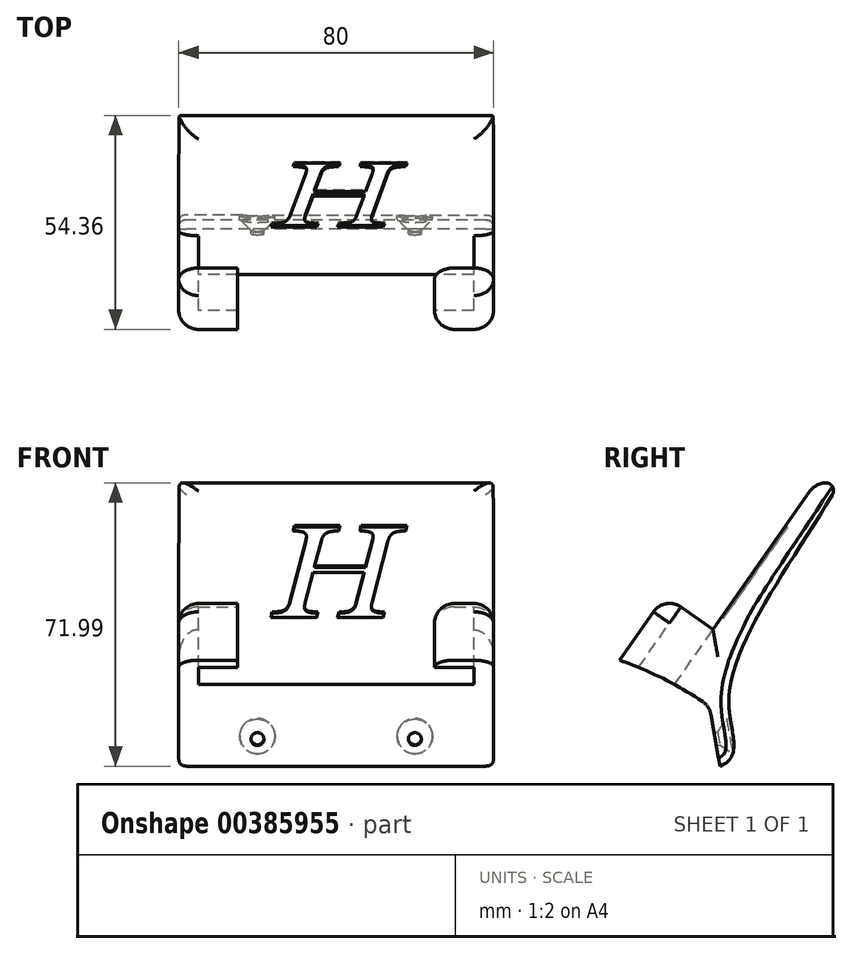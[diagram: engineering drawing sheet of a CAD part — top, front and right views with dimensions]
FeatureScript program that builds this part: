
annotation { "Feature Type Name" : "Feature", "Feature Type Description" : "" }
export const myFeature = defineFeature(function(context is Context, id is Id, definition is map)
    precondition{}
    {
        {
            var Q0;
            Q0=qCreatedBy(makeId("Right.planeOp"),FACE);
            var sketch = newSketch(context, id + "F0", { "sketchPlane" : qUnion([Q0])});
            skCircle(sketch, "E0", {"center": v(0, 0) * mm, "radius": 92 * mm});
            skLineSegment(sketch, "E1", {"start": v(53, 75.2) * mm, "end": v(53, 0) * mm});
            skLineSegment(sketch, "E2", {"start": v(0, 92) * mm, "end": v(0, 0) * mm});
            skLineSegment(sketch, "E3", {"start": v(0, 0) * mm, "end": v(53, 0) * mm});
            skLineSegment(sketch, "E4", {"start": v(41.65, 103.3) * mm, "end": v(53.94, 94.68) * mm});
            skLineSegment(sketch, "E5", {"start": v(53.94, 94.68) * mm, "end": v(44.15, 80.71) * mm});
            skLineSegment(sketch, "E6", {"start": v(53.94, 94.68) * mm, "end": v(81.44, 133.95) * mm});
            skLineSegment(sketch, "E7", {"start": v(81.44, 133.95) * mm, "end": v(85.54, 131.08) * mm});
            skLineSegment(sketch, "E8", {"start": v(53, 75.2) * mm, "end": v(61, 30.2) * mm});
            skLineSegment(sketch, "E9", {"start": v(41.65, 103.3) * mm, "end": v(30.18, 86.91) * mm});
            skFitSpline(sketch, "E10", {"points": [v(85.54, 131.08) * mm, v(57.95, 76.28) * mm, v(55.7, 59.99) * mm], "startDerivative": vector(-56.96, -95.44) * mm, "endDerivative": vector(-55.5, -22.93) * mm});
            skLineSegment(sketch, "E11", {"start": v(57.95, 76.28) * mm, "end": v(65.27, 35.08) * mm});
            skSolve(sketch);
        }
        {
            var Q0;
            {var subQ0=sQuery(id+"F0.wireOp",EDGE,"E1");var subQ1=sQuery(id+"F0.wireOp",EDGE,"E0");var subQ2=makeQuery(id+"F0.imprint","INTERSECT",VERTEX,{"derivedFrom":[subQ1,subQ0]});Q0=makeQuery(id+"F0.imprint","IMPRINT",FACE,{"disambiguationData":[TD([[makeQuery(id+"F0.imprint","IMPRINT",EDGE,{"disambiguationData":[TD([[subQ2,1.0]])],"derivedFrom":subQ1}),1.0]])]});}
            var Q1;
            {var subQ2=sQuery(id+"F0.wireOp",EDGE,"E5");Q1=makeQuery(id+"F0.imprint","IMPRINT",FACE,{"disambiguationData":[TD([[makeQuery(id+"F0.imprint","IMPRINT",EDGE,{"derivedFrom":subQ2}),1.0]])]});}
            var Q2;
            {var subQ0=sQuery(id+"F0.wireOp",EDGE,"VzTdmG4M-RMvp-aOg5-erqJ-xc0UWDuZk2gF");Q2=makeQuery(id+"F0.imprint","IMPRINT",FACE,{"disambiguationData":[TD([[makeQuery(id+"F0.imprint","IMPRINT",EDGE,{"derivedFrom":subQ0}),-1.0]])]});}
            var Q3;
            Q3=makeQuery(id+"F0.imprint","IMPRINT",FACE,{"disambiguationData":[TD([[makeQuery(id+"F0.imprint","IMPRINT",EDGE,{"derivedFrom":sQuery(id+"F0.wireOp",EDGE,"E4")}),-1.0]])]});
            extrude(context, id + "F1", {"entities" : qUnion([Q0, Q1, Q2, Q3]), "endBound" : BoundingType.SYMMETRIC, "depth" : 80 * mm});
        }
        {
            var Q0;
            Q0=makeQuery(id+"F1.opExtrude","SWEPT_FACE",FACE,{"disambiguationData":[OSD([sQuery(id+"F0.wireOp",EDGE,"E4")])]});
            var sketch = newSketch(context, id + "F2", { "sketchPlane" : qUnion([Q0])});
            skLineSegment(sketch, "E12.bottom", {"start": v(-35, -10.15) * mm, "end": v(35, -10.15) * mm});
            skLineSegment(sketch, "E12.top", {"start": v(-35, -20.15) * mm, "end": v(35, -20.15) * mm});
            skLineSegment(sketch, "E12.left", {"start": v(-35, -10.15) * mm, "end": v(-35, -20.15) * mm});
            skLineSegment(sketch, "E12.right", {"start": v(35, -10.15) * mm, "end": v(35, -20.15) * mm});
            skLineSegment(sketch, "E13.bottom", {"start": v(-25, -20.15) * mm, "end": v(25, -20.15) * mm});
            skLineSegment(sketch, "E13.top", {"start": v(-25, -25.15) * mm, "end": v(25, -25.15) * mm});
            skLineSegment(sketch, "E13.left", {"start": v(-25, -20.15) * mm, "end": v(-25, -25.15) * mm});
            skLineSegment(sketch, "E13.right", {"start": v(25, -20.15) * mm, "end": v(25, -25.15) * mm});
            skSolve(sketch);
        }
        {
            var Q0;
            Q0 = qSketchRegion(id + "F2", true);
            extrude(context, id + "F3", {"entities" : qUnion([Q0]), "operationType" : NewBodyOperationType.REMOVE, "depth" : -25.4 * mm});
        }
        {
            var Q0;
            Q0=makeQuery(id+"F3.boolean.opBoolean","MERGE",FACE,{"derivedFrom":[makeQuery(id+"F1.opExtrude","SWEPT_FACE",FACE,{"disambiguationData":[OSD([sQuery(id+"F0.wireOp",EDGE,"E6")])]}),makeQuery(id+"F3.opExtrude","SWEPT_FACE",FACE,{"disambiguationData":[OSD([sQuery(id+"F2.wireOp",EDGE,"E12.bottom")])]})]});
            var sketch = newSketch(context, id + "F4", { "sketchPlane" : qUnion([Q0])});
            skText(sketch, "E14", { "text": "H", "fontName": "NotoSerif-Italic.ttf"});
            const initialGuessF4  = {"E14": [-0.01575, 0.11234, 1, 0, 0.02865]};
            skSetInitialGuess(sketch, initialGuessF4);
            skSolve(sketch);
        }
        {
            var Q0;
            Q0 = qSketchRegion(id + "F4", true);
            extrude(context, id + "F5", {"entities" : qUnion([Q0]), "operationType" : NewBodyOperationType.REMOVE, "oppositeDirection" : true, "depth" : 0.5 * mm});
        }
        {
            var Q0;
            Q0=makeQuery(id+"F1.opExtrude","SWEPT_EDGE",EDGE,{"disambiguationData":[OSD([sQuery(id+"F0.wireOp",EDGE,"E0"),sQuery(id+"F0.wireOp",EDGE,"E1"),sQuery(id+"F0.wireOp",EDGE,"E8")])]});
            fillet(context, id + "F6", {"entities" : qUnion([Q0]), "radius" : 5 * mm, "tangentPropagation" : true, "allowEdgeOverflow" : false});
        }
        {
            var Q0;
            Q0=makeQuery(id+"F1.opExtrude","CAP_EDGE",EDGE,{"disambiguationData":[OSD([sQuery(id+"F0.wireOp",EDGE,"E6")])],"isStart":false});
            var Q1;
            Q1=makeQuery(id+"F1.opExtrude","SWEPT_EDGE",EDGE,{"disambiguationData":[OSD([sQuery(id+"F0.wireOp",EDGE,"E6"),sQuery(id+"F0.wireOp",EDGE,"E7")])]});
            var Q2;
            Q2=makeQuery(id+"F1.opExtrude","CAP_EDGE",EDGE,{"disambiguationData":[OSD([sQuery(id+"F0.wireOp",EDGE,"E6")])],"isStart":true});
            fillet(context, id + "F7", {"entities" : qUnion([Q0, Q1, Q2]), "radius" : 5 * mm, "tangentPropagation" : true, "allowEdgeOverflow" : false});
        }
        {
            var Q0;
            Q0=makeQuery(id+"F1.opExtrude","CAP_EDGE",EDGE,{"disambiguationData":[OSD([sQuery(id+"F0.wireOp",EDGE,"E4")])],"isStart":true});
            var Q1;
            {var subQ0=sQuery(id+"F0.wireOp",EDGE,"E9");var subQ1=sQuery(id+"F0.wireOp",EDGE,"E4");Q1=makeQuery(id+"F3.boolean.opBoolean","SPLIT",EDGE,{"disambiguationData":[TD([makeQuery(id+"F3.opExtrude","SWEPT_FACE",FACE,{"disambiguationData":[OSD([sQuery(id+"F2.wireOp",EDGE,"E13.left")])]})])],"derivedFrom":makeQuery(id+"F1.opExtrude","SWEPT_EDGE",EDGE,{"disambiguationData":[OSD([subQ1,subQ0])]})});}
            var Q2;
            {var subQ0=sQuery(id+"F0.wireOp",EDGE,"E9");var subQ1=sQuery(id+"F0.wireOp",EDGE,"E4");Q2=makeQuery(id+"F3.boolean.opBoolean","SPLIT",EDGE,{"disambiguationData":[TD([makeQuery(id+"F3.opExtrude","SWEPT_FACE",FACE,{"disambiguationData":[OSD([sQuery(id+"F2.wireOp",EDGE,"E13.right")])]})])],"derivedFrom":makeQuery(id+"F1.opExtrude","SWEPT_EDGE",EDGE,{"disambiguationData":[OSD([subQ1,subQ0])]})});}
            var Q3;
            Q3=makeQuery(id+"F1.opExtrude","CAP_EDGE",EDGE,{"disambiguationData":[OSD([sQuery(id+"F0.wireOp",EDGE,"E4")])],"isStart":false});
            fillet(context, id + "F8", {"entities" : qUnion([Q0, Q1, Q2, Q3]), "radius" : 5 * mm, "tangentPropagation" : true, "allowEdgeOverflow" : false});
        }
        {
            var Q0;
            Q0=makeQuery(id+"F3.boolean.opBoolean","COPY",EDGE,{"derivedFrom":makeQuery(id+"F3.opExtrude","SWEPT_EDGE",EDGE,{"disambiguationData":[OSD([sQuery(id+"F0.wireOp",EDGE,"E4"),sQuery(id+"F0.wireOp",EDGE,"E9"),sQuery(id+"F2.wireOp",EDGE,"E13.top"),sQuery(id+"F2.wireOp",EDGE,"E13.left")])]})});
            var Q1;
            Q1=makeQuery(id+"F3.boolean.opBoolean","COPY",EDGE,{"derivedFrom":makeQuery(id+"F3.opExtrude","SWEPT_EDGE",EDGE,{"disambiguationData":[OSD([sQuery(id+"F0.wireOp",EDGE,"E4"),sQuery(id+"F0.wireOp",EDGE,"E9"),sQuery(id+"F2.wireOp",EDGE,"E13.top"),sQuery(id+"F2.wireOp",EDGE,"E13.right")])]})});
            fillet(context, id + "F9", {"entities" : qUnion([Q0, Q1]), "radius" : 5 * mm, "tangentPropagation" : true, "allowEdgeOverflow" : false});
        }
        {
            var Q0;
            Q0=makeQuery(id+"F1.opExtrude","CAP_EDGE",EDGE,{"disambiguationData":[OSD([sQuery(id+"F0.wireOp",EDGE,"E9")])],"isStart":true});
            var Q1;
            Q1=makeQuery(id+"F1.opExtrude","CAP_EDGE",EDGE,{"disambiguationData":[OSD([sQuery(id+"F0.wireOp",EDGE,"E9")])],"isStart":false});
            fillet(context, id + "F10", {"entities" : qUnion([Q0, Q1]), "radius" : 5 * mm, "tangentPropagation" : true, "allowEdgeOverflow" : false});
        }
        {
            var Q0;
            Q0=makeQuery(id+"F7.opFillet","BLEND_EDGE",EDGE,{"blendedFrom":[makeQuery(id+"F1.opExtrude","SWEPT_EDGE",EDGE,{"disambiguationData":[OSD([sQuery(id+"F0.wireOp",EDGE,"E6"),sQuery(id+"F0.wireOp",EDGE,"E7")])]}),makeQuery(id+"F1.opExtrude","SWEPT_FACE",FACE,{"disambiguationData":[OSD([sQuery(id+"F0.wireOp",EDGE,"E10")])]})],"blendedInto":[makeQuery(id+"F1.opExtrude","SWEPT_FACE",FACE,{"disambiguationData":[OSD([sQuery(id+"F0.wireOp",EDGE,"E10")])]})]});
            fillet(context, id + "F11", {"entities" : qUnion([Q0]), "radius" : 2 * mm, "tangentPropagation" : true, "allowEdgeOverflow" : false});
        }
        {
            var Q0;
            Q0=makeQuery(id+"F1.opExtrude","CAP_EDGE",EDGE,{"disambiguationData":[OSD([sQuery(id+"F0.wireOp",EDGE,"E10")])],"isStart":false});
            var Q1;
            Q1=makeQuery(id+"F1.opExtrude","CAP_EDGE",EDGE,{"disambiguationData":[OSD([sQuery(id+"F0.wireOp",EDGE,"E10")])],"isStart":true});
            fillet(context, id + "F12", {"entities" : qUnion([Q0, Q1]), "radius" : 2 * mm, "rho" : 0.5, "crossSection" : FilletCrossSection.CONIC, "allowEdgeOverflow" : false});
        }
        {
            var Q0;
            Q0=makeQuery(id+"F1.opExtrude","SWEPT_FACE",FACE,{"disambiguationData":[OSD([sQuery(id+"F0.wireOp",EDGE,"E8")])]});
            cPlane(context, id + "F13", {"entities" : qUnion([Q0]), "cplaneType" : CPlaneType.OFFSET, "offset" : 5 * mm, "oppositeDirection" : true, "width" : 150 * mm, "height" : 150 * mm});
        }
        {
            var Q0;
            Q0=qCreatedBy(id+"F13.planeOp",FACE);
            var sketch = newSketch(context, id + "F14", { "sketchPlane" : qUnion([Q0])});
            skCircle(sketch, "E15", {"center": v(-20, 56.31) * mm, "radius": 3.58 * mm});
            skCircle(sketch, "E16", {"center": v(20, 56.31) * mm, "radius": 3.58 * mm});
            skSolve(sketch);
        }
        {
            var Q0;
            Q0=sQuery(id+"F14.wireOp",VERTEX,"E15.center");
            var Q1;
            Q1=sQuery(id+"F14.wireOp",VERTEX,"E16.center");
            var Q2;
            Q2=makeQuery(id+"F1.opExtrude","SWEPT_BODY",BODY,{"disambiguationData":[OSD([sQuery(id+"F0.wireOp",EDGE,"E0"),sQuery(id+"F0.wireOp",EDGE,"E4"),sQuery(id+"F0.wireOp",EDGE,"E6"),sQuery(id+"F0.wireOp",EDGE,"E7"),sQuery(id+"F0.wireOp",EDGE,"E8"),sQuery(id+"F0.wireOp",EDGE,"E9"),sQuery(id+"F0.wireOp",EDGE,"E10")])]});
            hole(context, id + "F15", {"style" : HoleStyle.C_SINK, "endStyle" : HoleEndStyle.THROUGH, "oppositeDirection" : true, "standardTappedOrClearance" : lookupTablePath({ "standard" : "ISO", "engagement" : "75%", "pitch" : "0.7 mm", "size" : "M4", "type" : "Tapped" }), "standardBlindInLast" : lookupTablePath({ "standard" : "ISO", "engagement" : "75%", "pitch" : "0.7 mm", "size" : "M4", "type" : "Tapped" }), "holeDiameter" : 3.3 * mm, "cSinkDiameter" : 8.96 * mm, "cSinkAngle" : 90 * degree, "showTappedDepth" : true, "isTappedThrough" : true, "tappedDepth" : 12 * mm, "tapClearance" : 3, "locations" : qUnion([Q0, Q1]), "scope" : qUnion([Q2]), "majorDiameter" : 4 * mm});
        }
    });
